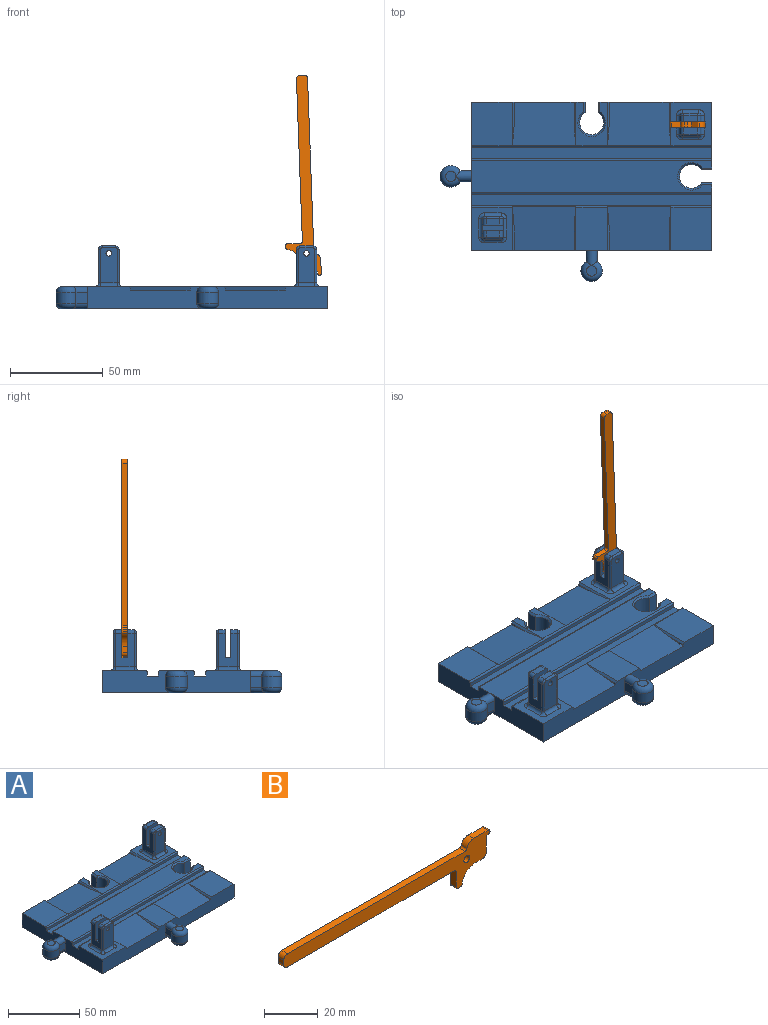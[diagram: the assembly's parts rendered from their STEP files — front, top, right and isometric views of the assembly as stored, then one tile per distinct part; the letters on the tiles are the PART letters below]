
ASSEMBLY  parts=2 mates=1
PART A: 156 faces, bbox 146.9x96.9x34.2 mm
  f0: plane 12.13x1mm, normal (-1,0,0), area 6.1mm2, adj f22,f135,f150
  f1: plane 12.13x1mm, normal (1,0,0), area 6.1mm2, adj f12,f134,f154
  f2: plane 12.13x1mm, normal (1,0,0), area 6.1mm2, adj f23,f133,f146
  f3: plane 12.13x1mm, normal (-1,0,0), area 6.1mm2, adj f23,f133,f144
  f4: plane 7.14x3.63mm, normal (0,0,1), area 25.9mm2, adj f81,f88,f95,f115
  f5: plane 7.14x3.63mm, normal (0,0,1), area 25.9mm2, adj f78,f92,f93,f98
  f6: plane 18x10.25mm, normal (1,0,0), area 145.5mm2, adj f78,f79,f80,f91,f93,f96,f105,f124
  f7: plane 23.25x22.14mm, normal (0,0,1), area 276.5mm2, adj f13,f21,f116,f117,f118,f119,f120,f121
  f8: plane 23.25x22.14mm, normal (0,0,1), area 276.5mm2, adj f17,f22,f124,f125,f126,f127,f128,f129
  f9: plane 23.25x17mm, normal (0,0,1), area 184.1mm2, adj f22,f23,f56,f57,f58,f136,f144,f148
  f10: plane 23.25x22.14mm, normal (0,0,1), area 514.9mm2, adj f12,f16,f137,f152
  f11: plane 23.25x17mm, normal (0,0,1), area 395.3mm2, adj f12,f13,f137,f140,f154
  f12: plane 65x12mm, normal (0,-1,0), area 682.2mm2, adj f1,f10,f11,f16,f26,f35,f43,f45
  f13: plane 65x12mm, normal (0,-1,0), area 682.2mm2, adj f7,f11,f21,f26,f33,f43,f45,f65
  f14: plane 23.25x22.14mm, normal (0,0,1), area 514.9mm2, adj f23,f24,f136,f146
  f15: plane 130x17.5mm, normal (0,0,1), area 2063.9mm2, adj f16,f17,f21,f24,f50,f51,f52,f138
  f16: plane 36.5x12mm, normal (1,0,0), area 418.6mm2, adj f10,f12,f15,f26,f29,f47,f52,f62
  f17: plane 36.5x12mm, normal (1,0,0), area 418.6mm2, adj f8,f15,f22,f26,f27,f49,f50,f59
  f18: plane 5.6x5.6mm, normal (0,0,1), area 24.6mm2, adj f42
  f19: plane 5.6x5.6mm, normal (0,0,-1), area 24.6mm2, adj f39
  f20: plane 5.6x5.6mm, normal (0,0,-1), area 24.6mm2, adj f44
  f21: plane 40x12mm, normal (-1,0,0), area 429.4mm2, adj f7,f13,f15,f26,f37,f40,f41,f62
  f22: plane 61.5x12mm, normal (0,1,0), area 671.3mm2, adj f0,f8,f9,f17,f26,f32,f54,f58
  f23: plane 61.5x12mm, normal (0,1,0), area 671.3mm2, adj f2,f3,f9,f14,f24,f26,f30,f53
  f24: plane 40x12mm, normal (-1,0,0), area 429.4mm2, adj f14,f15,f23,f26,f38,f40,f41,f59
  f25: plane 5.6x5.6mm, normal (0,0,1), area 24.6mm2, adj f46
  f26: plane 130x80mm, normal (0,0,-1), area 9977.8mm2, adj f12,f13,f16,f17,f21,f22,f23,f24
  f27: plane 10x5.63mm, normal (0,-1,0), area 56.3mm2, adj f17,f28,f49,f50
  f28: cylinder r=6.45mm len=12.9mm, axis (0,0,1), area 331.3mm2, adj f27,f29,f48,f51
  f29: plane 10x5.63mm, normal (0,1,0), area 56.3mm2, adj f16,f28,f47,f52
  f30: plane 10x5.63mm, normal (1,0,0), area 56.3mm2, adj f23,f31,f53,f56
  f31: cylinder r=6.45mm len=12.9mm, axis (0,0,1), area 331.3mm2, adj f30,f32,f55,f57
  f32: plane 10x5.63mm, normal (-1,0,0), area 56.3mm2, adj f22,f31,f54,f58
  f33: plane 6.14x6mm, normal (-1,0,0), area 36.8mm2, adj f13,f34,f43,f45
  f34: cylinder r=5.8mm len=11.6mm, axis (0,0,1), area 180.8mm2, adj f33,f35,f44,f46
  f35: plane 6.14x6mm, normal (1,0,0), area 36.8mm2, adj f12,f34,f43,f45
  f36: cylinder r=5.8mm len=11.6mm, axis (0,0,1), area 180.8mm2, adj f37,f38,f39,f42
  f37: plane 6.14x6mm, normal (0,-1,0), area 36.8mm2, adj f21,f36,f40,f41
  f38: plane 6.14x6mm, normal (0,1,0), area 36.8mm2, adj f24,f36,f40,f41
  f39: torus R=2.8mm, axis (0,0,1), area 120.8mm2, adj f19,f36,f40
  f40: cylinder r=3mm len=8.3mm, axis (1,0,0), area 64.5mm2, adj f21,f24,f37,f38,f39
  f41: cylinder r=3mm len=8.3mm, axis (1,0,0), area 64.5mm2, adj f21,f24,f37,f38,f42
  f42: torus R=2.8mm, axis (0,0,1), area 120.8mm2, adj f18,f36,f41
  f43: cylinder r=3mm len=8.3mm, axis (0,1,0), area 64.5mm2, adj f12,f13,f33,f35,f44
  f44: torus R=2.8mm, axis (0,0,1), area 120.8mm2, adj f20,f34,f43
  f45: cylinder r=3mm len=8.3mm, axis (0,1,0), area 64.5mm2, adj f12,f13,f33,f35,f46
  f46: torus R=2.8mm, axis (0,0,1), area 120.8mm2, adj f25,f34,f45
  f47: plane 5.66x1.03mm, normal (0,0.71,-0.71), area 7.6mm2, adj f16,f26,f29,f48
  f48: cone r=7.45mm half-angle=45deg, axis (0,0,-1), area 49.7mm2, adj f26,f28,f47,f49
  f49: plane 5.66x1.03mm, normal (0,-0.71,-0.71), area 7.6mm2, adj f17,f26,f27,f48
  f50: plane 5.66x1.03mm, normal (0,-0.71,0.71), area 7.6mm2, adj f15,f17,f27,f51
  f51: cone r=6.45mm half-angle=45deg, axis (0,0,1), area 49.7mm2, adj f15,f28,f50,f52
  f52: plane 5.66x1.03mm, normal (0,0.71,0.71), area 7.6mm2, adj f15,f16,f29,f51
  f53: plane 5.66x1.03mm, normal (0.71,0,-0.71), area 7.6mm2, adj f23,f26,f30,f55
  f54: plane 5.66x1.03mm, normal (-0.71,0,-0.71), area 7.6mm2, adj f22,f26,f32,f55
  f55: cone r=7.45mm half-angle=45deg, axis (0,0,-1), area 49.7mm2, adj f26,f31,f53,f54
  f56: plane 5.66x1.03mm, normal (0.71,0,0.71), area 7.6mm2, adj f9,f23,f30,f57
  f57: cone r=6.45mm half-angle=45deg, axis (0,0,1), area 49.7mm2, adj f9,f31,f56,f58
  f58: plane 5.66x1.03mm, normal (-0.71,0,0.71), area 7.6mm2, adj f9,f22,f32,f57
  f59: plane 130x2mm, normal (0,-1,0), area 260mm2, adj f17,f24,f61,f136
  f60: plane 130x2mm, normal (0,1,0), area 260mm2, adj f17,f24,f61,f139
  f61: plane 130x6mm, normal (0,0,1), area 780mm2, adj f17,f24,f59,f60
  f62: plane 130x2mm, normal (0,-1,0), area 260mm2, adj f16,f21,f64,f138
  f63: plane 130x2mm, normal (0,1,0), area 260mm2, adj f16,f21,f64,f137
  f64: plane 130x6mm, normal (0,0,1), area 780mm2, adj f16,f21,f62,f63
  f65: plane 12.13x1mm, normal (-1,0,0), area 6.1mm2, adj f13,f132,f140
  f66: plane 12.13x1mm, normal (1,0,0), area 6.1mm2, adj f13,f132,f142
  f67: plane 12.13x1mm, normal (-1,0,0), area 6.1mm2, adj f12,f134,f152
  f68: plane 12.13x1mm, normal (1,0,0), area 6.1mm2, adj f22,f135,f148
  f69: plane 19x9.14mm, normal (0,-1,0), area 166.2mm2, adj f84,f106,f107,f108,f109,f110,f116
  f70: plane 18x10.25mm, normal (1,0,0), area 145.5mm2, adj f81,f82,f83,f88,f94,f107,f111,f119
  f71: plane 19x9.14mm, normal (0,1,0), area 166.2mm2, adj f85,f111,f112,f113,f114,f115,f123
  f72: plane 18x10.25mm, normal (-1,0,0), area 145.5mm2, adj f81,f82,f83,f89,f95,f106,f112,f120
  f73: plane 7.14x3.63mm, normal (0,0,1), area 25.9mm2, adj f82,f89,f94,f110
  f74: plane 19x9.14mm, normal (0,1,0), area 166.2mm2, adj f87,f96,f97,f98,f99,f100,f127
  f75: plane 18x10.25mm, normal (-1,0,0), area 145.5mm2, adj f78,f79,f80,f90,f92,f100,f101,f131
  f76: plane 19x9.14mm, normal (0,-1,0), area 166.2mm2, adj f86,f101,f102,f103,f104,f105,f128
  f77: plane 7.14x3.63mm, normal (0,0,1), area 25.9mm2, adj f79,f90,f91,f103
  f78: plane 15x11.14mm, normal (0,-1,0), area 158.4mm2, adj f5,f6,f75,f80,f87,f92,f93
  f79: plane 15x11.14mm, normal (0,1,0), area 158.4mm2, adj f6,f75,f77,f80,f86,f90,f91
  f80: plane 11.14x3mm, normal (0,0,1), area 33.4mm2, adj f6,f75,f78,f79
  f81: plane 15x11.14mm, normal (0,-1,0), area 158.4mm2, adj f4,f70,f72,f83,f85,f88,f95
  f82: plane 15x11.14mm, normal (0,1,0), area 158.4mm2, adj f70,f72,f73,f83,f84,f89,f94
  f83: plane 11.14x3mm, normal (0,0,1), area 33.4mm2, adj f70,f72,f81,f82
  f84: cylinder r=1.5mm len=4.63mm, axis (0,-1,0), area 43.6mm2, adj f69,f82
  f85: cylinder r=1.5mm len=4.63mm, axis (0,-1,0), area 43.6mm2, adj f71,f81
  f86: cylinder r=1.5mm len=4.63mm, axis (0,-1,0), area 43.6mm2, adj f76,f79
  f87: cylinder r=1.5mm len=4.63mm, axis (0,-1,0), area 43.6mm2, adj f74,f78
  f88: cylinder r=2mm len=3.63mm, axis (0,-1,0), area 11.4mm2, adj f4,f70,f81,f113
  f89: cylinder r=2mm len=3.63mm, axis (0,1,0), area 11.4mm2, adj f72,f73,f82,f108
  f90: cylinder r=2mm len=3.63mm, axis (0,1,0), area 11.4mm2, adj f75,f77,f79,f102
  f91: cylinder r=2mm len=3.63mm, axis (0,-1,0), area 11.4mm2, adj f6,f77,f79,f104
  f92: cylinder r=2mm len=3.63mm, axis (0,1,0), area 11.4mm2, adj f5,f75,f78,f99
  f93: cylinder r=2mm len=3.63mm, axis (0,-1,0), area 11.4mm2, adj f5,f6,f78,f97
  f94: cylinder r=2mm len=3.63mm, axis (0,-1,0), area 11.4mm2, adj f70,f73,f82,f109
  f95: cylinder r=2mm len=3.63mm, axis (0,1,0), area 11.4mm2, adj f4,f72,f81,f114
  f96: cylinder r=1mm len=18mm, axis (0,0,-1), area 28.3mm2, adj f6,f74,f97,f125
  f97: torus R=1mm, axis (0,1,0), area 4mm2, adj f74,f93,f96,f98
  f98: cylinder r=1mm len=7.14mm, axis (1,0,0), area 11.2mm2, adj f5,f74,f97,f99
  f99: torus R=1mm, axis (0,1,0), area 4mm2, adj f74,f92,f98,f100
  f100: cylinder r=1mm len=18mm, axis (0,0,1), area 28.3mm2, adj f74,f75,f99,f129
  f101: cylinder r=1mm len=18mm, axis (0,0,-1), area 28.3mm2, adj f75,f76,f102,f130
  f102: torus R=1mm, axis (0,1,0), area 4mm2, adj f76,f90,f101,f103
  f103: cylinder r=1mm len=7.14mm, axis (-1,0,0), area 11.2mm2, adj f76,f77,f102,f104
  f104: torus R=1mm, axis (0,1,0), area 4mm2, adj f76,f91,f103,f105
  f105: cylinder r=1mm len=18mm, axis (0,0,1), area 28.3mm2, adj f6,f76,f104,f126
  f106: cylinder r=1mm len=18mm, axis (0,0,-1), area 28.3mm2, adj f69,f72,f108,f118
  f107: cylinder r=1mm len=18mm, axis (0,0,-1), area 28.3mm2, adj f69,f70,f109,f117
  f108: torus R=1mm, axis (0,1,0), area 4mm2, adj f69,f89,f106,f110
  f109: torus R=1mm, axis (0,1,0), area 4mm2, adj f69,f94,f107,f110
  f110: cylinder r=1mm len=7.14mm, axis (-1,0,0), area 11.2mm2, adj f69,f73,f108,f109
  f111: cylinder r=1mm len=18mm, axis (0,0,-1), area 28.3mm2, adj f70,f71,f113,f121
  f112: cylinder r=1mm len=18mm, axis (0,0,-1), area 28.3mm2, adj f71,f72,f114,f122
  f113: torus R=1mm, axis (0,-1,0), area 4mm2, adj f71,f88,f111,f115
  f114: torus R=1mm, axis (0,-1,0), area 4mm2, adj f71,f95,f112,f115
  f115: cylinder r=1mm len=7.14mm, axis (1,0,0), area 11.2mm2, adj f4,f71,f113,f114
  f116: cylinder r=2mm len=9.14mm, axis (1,0,0), area 28.7mm2, adj f7,f69,f117,f118
  f117: torus R=3mm, axis (0,0,1), area 8.5mm2, adj f7,f107,f116,f119
  f118: torus R=3mm, axis (0,0,1), area 8.5mm2, adj f7,f106,f116,f120
  f119: cylinder r=2mm len=10.25mm, axis (0,1,0), area 32.2mm2, adj f7,f70,f117,f121
  f120: cylinder r=2mm len=10.25mm, axis (0,-1,0), area 32.2mm2, adj f7,f72,f118,f122
  f121: torus R=3mm, axis (0,0,1), area 8.5mm2, adj f7,f111,f119,f123
  f122: torus R=3mm, axis (0,0,1), area 8.5mm2, adj f7,f112,f120,f123
  f123: cylinder r=2mm len=9.14mm, axis (-1,0,0), area 28.7mm2, adj f7,f71,f121,f122
  f124: cylinder r=2mm len=10.25mm, axis (0,1,0), area 32.2mm2, adj f6,f8,f125,f126
  f125: torus R=3mm, axis (0,0,1), area 8.5mm2, adj f8,f96,f124,f127
  f126: torus R=3mm, axis (0,0,1), area 8.5mm2, adj f8,f105,f124,f128
  f127: cylinder r=2mm len=9.14mm, axis (-1,0,0), area 28.7mm2, adj f8,f74,f125,f129
  f128: cylinder r=2mm len=9.14mm, axis (1,0,0), area 28.7mm2, adj f8,f76,f126,f130
  f129: torus R=3mm, axis (0,0,1), area 8.5mm2, adj f8,f100,f127,f131
  f130: torus R=3mm, axis (0,0,1), area 8.5mm2, adj f8,f101,f128,f131
  f131: cylinder r=2mm len=10.25mm, axis (0,-1,0), area 32.2mm2, adj f8,f75,f129,f130
  f132: plane 34.4x23.62mm, normal (0,-0.08,1), area 776.3mm2, adj f13,f65,f66,f137,f140,f141,f142,f143
  f133: plane 34.4x23.62mm, normal (0,0.08,1), area 776.3mm2, adj f2,f3,f23,f136,f144,f145,f146,f147
  f134: plane 34.4x23.62mm, normal (0,-0.08,1), area 776.3mm2, adj f1,f12,f67,f137,f152,f153,f154,f155
  f135: plane 34.4x23.62mm, normal (0,0.08,1), area 776.3mm2, adj f0,f22,f68,f136,f148,f149,f150,f151
  f136: cylinder r=1mm len=130mm, axis (1,0,0), area 181.2mm2, adj f8,f9,f14,f17,f24,f59,f133,f135
  f137: cylinder r=1mm len=130mm, axis (-1,0,0), area 181.2mm2, adj f7,f10,f11,f16,f21,f63,f132,f134
  f138: cylinder r=1mm len=130mm, axis (1,0,0), area 204.2mm2, adj f15,f16,f21,f62
  f139: cylinder r=1mm len=130mm, axis (-1,0,0), area 204.2mm2, adj f15,f17,f24,f60
  f140: plane 23.25x1mm, normal (-0.71,0,0.71), area 25.7mm2, adj f11,f13,f65,f132,f141
  f141: cone r=1mm half-angle=45deg, axis (1,0,0), area 0mm2, adj f132,f137,f140
  f142: plane 23.25x1mm, normal (0.71,0,0.71), area 25.7mm2, adj f7,f13,f66,f132,f143
  f143: cone r=1mm half-angle=45deg, axis (-1,0,0), area 0mm2, adj f132,f137,f142
  f144: plane 23.25x1mm, normal (-0.71,0,0.71), area 25.7mm2, adj f3,f9,f23,f133,f145
  f145: cone r=1mm half-angle=45deg, axis (1,0,0), area 0mm2, adj f133,f136,f144
  f146: plane 23.25x1mm, normal (0.71,0,0.71), area 25.7mm2, adj f2,f14,f23,f133,f147
  f147: cone r=1mm half-angle=45deg, axis (-1,0,0), area 0mm2, adj f133,f136,f146
  f148: plane 23.25x1mm, normal (0.71,0,0.71), area 25.7mm2, adj f9,f22,f68,f135,f149
  f149: cone r=1mm half-angle=45deg, axis (-1,0,0), area 0mm2, adj f135,f136,f148
  f150: plane 23.25x1mm, normal (-0.71,0,0.71), area 25.7mm2, adj f0,f8,f22,f135,f151
  f151: cone r=1mm half-angle=45deg, axis (1,0,0), area 0mm2, adj f135,f136,f150
  f152: plane 23.25x1mm, normal (-0.71,0,0.71), area 25.7mm2, adj f10,f12,f67,f134,f153
  f153: cone r=1mm half-angle=45deg, axis (1,0,0), area 0mm2, adj f134,f137,f152
  f154: plane 23.25x1mm, normal (0.71,0,0.71), area 25.7mm2, adj f1,f11,f12,f134,f155
  f155: cone r=1mm half-angle=45deg, axis (-1,0,0), area 0mm2, adj f134,f137,f154
PART B: 24 faces, bbox 108.5x3x18.6 mm
  f0: cylinder r=3.57mm len=3.49mm, axis (0,1,0), area 14.5mm2, adj f14,f16,f17,f21
  f1: plane 93.39x3mm, normal (0,0,1), area 280.2mm2, adj f2,f16,f17,f21
  f2: cylinder r=2mm len=3mm, axis (0,1,0), area 9.4mm2, adj f1,f3,f16,f17
  f3: plane 3x2mm, normal (-1,0,0), area 6mm2, adj f2,f4,f16,f17
  f4: cylinder r=2mm len=3mm, axis (0,1,0), area 9.4mm2, adj f3,f5,f16,f17
  f5: plane 87.71x3mm, normal (0,0,-1), area 263.1mm2, adj f4,f16,f17,f18
  f6: plane 7x3mm, normal (-1,0,0), area 21mm2, adj f16,f17,f18,f22
  f7: plane 3x1.21mm, normal (0,0,-1), area 3.6mm2, adj f16,f17,f22,f23
  f8: cylinder r=7mm len=6.95mm, axis (0,1,0), area 30.4mm2, adj f9,f16,f17,f23
  f9: plane 3.67x3mm, normal (0,0,-1), area 11mm2, adj f8,f10,f16,f17
  f10: cylinder r=2mm len=3mm, axis (0,1,0), area 9.4mm2, adj f9,f11,f16,f17
  f11: plane 7.57x3mm, normal (1,0,0), area 22.7mm2, adj f10,f12,f16,f17
  f12: plane 3x1mm, normal (0,0,-1), area 3mm2, adj f11,f16,f17,f19
  f13: plane 3x0mm, normal (1,0,0), area 0mm2, adj f16,f17,f19,f20
  f14: plane 7.67x3mm, normal (0,0,1), area 23mm2, adj f0,f16,f17,f20
  f15: cylinder r=1.5mm len=3mm, axis (0,1,0), area 28.3mm2, adj f16,f17
  f16: plane 108.53x18.57mm, normal (0,-1,0), area 731.1mm2, adj f0,f1,f2,f3,f4,f5,f6,f7
  f17: plane 108.53x18.57mm, normal (0,1,0), area 731.1mm2, adj f0,f1,f2,f3,f4,f5,f6,f7
  f18: cylinder r=1mm len=3mm, axis (0,1,0), area 4.7mm2, adj f5,f6,f16,f17
  f19: cylinder r=1mm len=3mm, axis (0,1,0), area 4.7mm2, adj f12,f13,f16,f17
  f20: cylinder r=1mm len=3mm, axis (0,1,0), area 4.7mm2, adj f13,f14,f16,f17
  f21: cylinder r=1mm len=3mm, axis (0,1,0), area 4.1mm2, adj f0,f1,f16,f17
  f22: cylinder r=1mm len=3mm, axis (0,-1,0), area 4.7mm2, adj f6,f7,f16,f17
  f23: cylinder r=1mm len=3mm, axis (0,1,0), area 4.3mm2, adj f7,f8,f16,f17
PLACE A t=(-1.62,0,8.53)mm fixed
PLACE B rot(axis=(0,1,0),87.9deg) t=(19.88,0,90.83)mm
MATE revolute B.f15 <-> A.f86  axis (0,-1,0) through (51.81,26.38,38.53)mm
